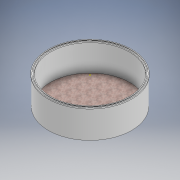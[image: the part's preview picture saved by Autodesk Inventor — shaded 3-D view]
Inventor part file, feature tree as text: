
AUTODESK INVENTOR PART (.ipt)
format: ipt  version: 2022 (Build 260153000, 153)  size: 156,160 bytes
history: native  units: mm
features: sketch x5, extrude x4
ambient origin geometry x8: Origin, YZ Plane, XZ Plane, XY Plane, X Axis, Y Axis, Z Axis, Center Point
bodies: Solid1 (feature_tree)
feature tree (9):
  extrude  "Floor"  Depth=1600.0mm TaperAngle=0.0deg
  extrude  "Wall"  Depth=4750.0mm
  sketch  "Sketch3"  dims[d6=50.0mm d7=0.0mm d8=20.0mm d9=0.0mm]
  extrude  "Extrusion3"  Depth=20.0mm TaperAngle=0.0deg
  extrude  "Extrusion4"  [1 undecoded]
  sketch  "Sketch1"  dims[d0=50.0mm d1=0.0mm d2=1600.0mm d3=0.0mm]
  sketch  "Sketch2"  dims[d4=5050.0mm d5=4750.0mm]
  sketch  "Sketch4"
  sketch  "Sketch5"
note: 1 required parameter value undecoded (feature->parameter linkage not recoverable at this tier; creation-order binding heuristic only, values carry confidence <= 0.55)
